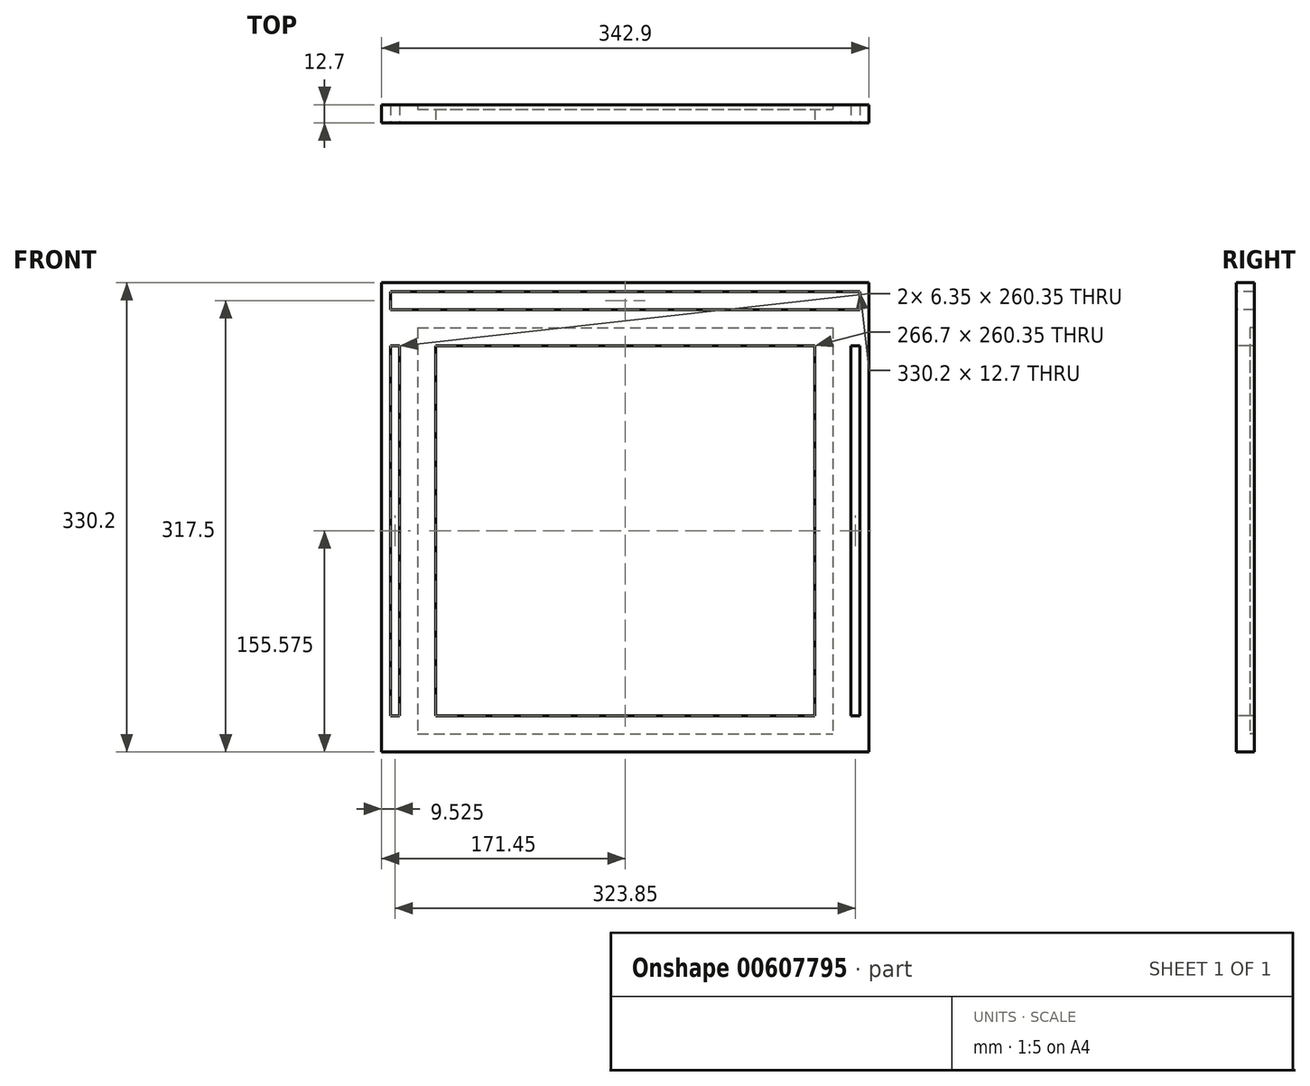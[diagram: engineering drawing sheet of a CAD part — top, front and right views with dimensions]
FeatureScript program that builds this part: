
annotation { "Feature Type Name" : "Feature", "Feature Type Description" : "" }
export const myFeature = defineFeature(function(context is Context, id is Id, definition is map)
    precondition{}
    {
        {
            var Q0;
            Q0=qCreatedBy(makeId("Front.planeOp"),FACE);
            var sketch = newSketch(context, id + "F0", { "sketchPlane" : qUnion([Q0])});
            skLineSegment(sketch, "E0.bottom", {"start": v(0, 0) * mm, "end": v(342.9, 0) * mm});
            skLineSegment(sketch, "E0.top", {"start": v(0, 330.2) * mm, "end": v(342.9, 330.2) * mm});
            skLineSegment(sketch, "E0.left", {"start": v(0, 0) * mm, "end": v(0, 330.2) * mm});
            skLineSegment(sketch, "E0.right", {"start": v(342.9, 0) * mm, "end": v(342.9, 330.2) * mm});
            skSolve(sketch);
        }
        {
            var Q0;
            Q0=makeQuery(id+"F0.imprint","IMPRINT",FACE,{"disambiguationData":[TD([[makeQuery(id+"F0.imprint","IMPRINT",EDGE,{"derivedFrom":sQuery(id+"F0.wireOp",EDGE,"E0.bottom")}),1.0]])]});
            extrude(context, id + "F1", {"entities" : qUnion([Q0]), "depth" : 12.7 * mm, "offsetDistance" : 25.4 * mm});
        }
        {
            var Q0;
            Q0=makeQuery(id+"F1.opExtrude","CAP_FACE",FACE,{"disambiguationData":[OSD([sQuery(id+"F0.wireOp",EDGE,"E0.bottom"),sQuery(id+"F0.wireOp",EDGE,"E0.top"),sQuery(id+"F0.wireOp",EDGE,"E0.left"),sQuery(id+"F0.wireOp",EDGE,"E0.right")])],"isStart":false});
            var sketch = newSketch(context, id + "F2", { "sketchPlane" : qUnion([Q0])});
            skLineSegment(sketch, "E1", {"start": v(0, 0) * mm, "end": v(25.4, 0) * mm});
            skLineSegment(sketch, "E2", {"start": v(25.4, 0) * mm, "end": v(25.4, 12.7) * mm});
            skLineSegment(sketch, "E3", {"start": v(25.4, 12.7) * mm, "end": v(317.5, 12.7) * mm});
            skLineSegment(sketch, "E4", {"start": v(317.5, 12.7) * mm, "end": v(317.5, 298.45) * mm});
            skLineSegment(sketch, "E5", {"start": v(317.5, 298.45) * mm, "end": v(25.4, 298.45) * mm});
            skLineSegment(sketch, "E6", {"start": v(25.4, 12.7) * mm, "end": v(25.4, 298.45) * mm});
            skSolve(sketch);
        }
        {
            var Q0;
            Q0=makeQuery(id+"F2.imprint","IMPRINT",FACE,{"disambiguationData":[TD([[makeQuery(id+"F2.imprint","IMPRINT",EDGE,{"derivedFrom":sQuery(id+"F2.wireOp",EDGE,"E3")}),1.0]])]});
            extrude(context, id + "F3", {"entities" : qUnion([Q0]), "operationType" : NewBodyOperationType.REMOVE, "oppositeDirection" : true, "depth" : 12.7 * mm, "offsetDistance" : 25.4 * mm});
        }
        {
            var Q0;
            Q0=makeQuery(id+"F1.opExtrude","CAP_FACE",FACE,{"disambiguationData":[OSD([sQuery(id+"F0.wireOp",EDGE,"E0.bottom"),sQuery(id+"F0.wireOp",EDGE,"E0.top"),sQuery(id+"F0.wireOp",EDGE,"E0.left"),sQuery(id+"F0.wireOp",EDGE,"E0.right")])],"isStart":false});
            var sketch = newSketch(context, id + "F4", { "sketchPlane" : qUnion([Q0])});
            skLineSegment(sketch, "E7", {"start": v(0, 330.2) * mm, "end": v(6.35, 330.2) * mm});
            skLineSegment(sketch, "E8", {"start": v(6.35, 330.2) * mm, "end": v(6.35, 323.85) * mm});
            skLineSegment(sketch, "E9", {"start": v(6.35, 323.85) * mm, "end": v(6.35, 311.15) * mm});
            skLineSegment(sketch, "E10", {"start": v(6.35, 311.15) * mm, "end": v(336.55, 311.15) * mm});
            skLineSegment(sketch, "E11", {"start": v(336.55, 311.15) * mm, "end": v(336.55, 323.85) * mm});
            skLineSegment(sketch, "E12", {"start": v(336.55, 323.85) * mm, "end": v(6.35, 323.85) * mm});
            skLineSegment(sketch, "E13", {"start": v(6.35, 311.15) * mm, "end": v(6.35, 285.75) * mm});
            skLineSegment(sketch, "E14", {"start": v(6.35, 285.75) * mm, "end": v(6.35, 25.4) * mm});
            skLineSegment(sketch, "E15", {"start": v(6.35, 25.4) * mm, "end": v(12.7, 25.4) * mm});
            skLineSegment(sketch, "E16", {"start": v(12.7, 25.4) * mm, "end": v(12.7, 285.75) * mm});
            skLineSegment(sketch, "E17", {"start": v(12.7, 285.75) * mm, "end": v(6.35, 285.75) * mm});
            skLineSegment(sketch, "E18", {"start": v(336.55, 311.15) * mm, "end": v(336.55, 285.75) * mm});
            skLineSegment(sketch, "E19", {"start": v(336.55, 285.75) * mm, "end": v(330.2, 285.75) * mm});
            skLineSegment(sketch, "E20", {"start": v(330.2, 285.75) * mm, "end": v(330.2, 25.4) * mm});
            skLineSegment(sketch, "E21", {"start": v(330.2, 25.4) * mm, "end": v(336.55, 25.4) * mm});
            skLineSegment(sketch, "E22", {"start": v(336.55, 25.4) * mm, "end": v(336.55, 285.75) * mm});
            skSolve(sketch);
        }
        {
            var Q0;
            Q0=makeQuery(id+"F4.imprint","IMPRINT",FACE,{"disambiguationData":[TD([[makeQuery(id+"F4.imprint","IMPRINT",EDGE,{"derivedFrom":sQuery(id+"F4.wireOp",EDGE,"E9")}),1.0]])]});
            var Q1;
            Q1=makeQuery(id+"F4.imprint","IMPRINT",FACE,{"disambiguationData":[TD([[makeQuery(id+"F4.imprint","IMPRINT",EDGE,{"derivedFrom":sQuery(id+"F4.wireOp",EDGE,"E14")}),1.0]])]});
            var Q2;
            Q2=makeQuery(id+"F4.imprint","IMPRINT",FACE,{"disambiguationData":[TD([[makeQuery(id+"F4.imprint","IMPRINT",EDGE,{"derivedFrom":sQuery(id+"F4.wireOp",EDGE,"E19")}),1.0]])]});
            extrude(context, id + "F5", {"entities" : qUnion([Q0, Q1, Q2]), "operationType" : NewBodyOperationType.REMOVE, "oppositeDirection" : true, "depth" : 12.7 * mm, "offsetDistance" : 25.4 * mm});
        }
        {
            var Q0;
            Q0=makeQuery(id+"F3.boolean.opBoolean","COPY",FACE,{"derivedFrom":makeQuery(id+"F3.opExtrude","SWEPT_FACE",FACE,{"disambiguationData":[OSD([sQuery(id+"F2.wireOp",EDGE,"E3")])]})});
            var sketch = newSketch(context, id + "F6", { "sketchPlane" : qUnion([Q0])});
            skLineSegment(sketch, "E23.bottom", {"start": v(25.4, -12.7) * mm, "end": v(317.5, -12.7) * mm});
            skLineSegment(sketch, "E23.top", {"start": v(25.4, -3.18) * mm, "end": v(317.5, -3.18) * mm});
            skLineSegment(sketch, "E23.left", {"start": v(25.4, -12.7) * mm, "end": v(25.4, -3.18) * mm});
            skLineSegment(sketch, "E23.right", {"start": v(317.5, -12.7) * mm, "end": v(317.5, -3.18) * mm});
            skSolve(sketch);
        }
        {
            var Q0;
            Q0=makeQuery(id+"F6.imprint","IMPRINT",FACE,{"disambiguationData":[TD([[makeQuery(id+"F6.imprint","IMPRINT",EDGE,{"derivedFrom":sQuery(id+"F6.wireOp",EDGE,"E23.bottom")}),1.0]])]});
            extrude(context, id + "F7", {"entities" : qUnion([Q0]), "operationType" : NewBodyOperationType.ADD, "depth" : 12.7 * mm, "offsetDistance" : 25.4 * mm});
        }
        {
            var Q0;
            Q0=makeQuery(id+"F3.boolean.opBoolean","COPY",FACE,{"derivedFrom":makeQuery(id+"F3.opExtrude","SWEPT_FACE",FACE,{"disambiguationData":[OSD([sQuery(id+"F2.wireOp",EDGE,"E5")])]})});
            var sketch = newSketch(context, id + "F8", { "sketchPlane" : qUnion([Q0])});
            skLineSegment(sketch, "E24.bottom", {"start": v(25.4, 12.7) * mm, "end": v(317.5, 12.7) * mm});
            skLineSegment(sketch, "E24.top", {"start": v(25.4, 3.18) * mm, "end": v(317.5, 3.18) * mm});
            skLineSegment(sketch, "E24.left", {"start": v(25.4, 12.7) * mm, "end": v(25.4, 3.18) * mm});
            skLineSegment(sketch, "E24.right", {"start": v(317.5, 12.7) * mm, "end": v(317.5, 3.18) * mm});
            skSolve(sketch);
        }
        {
            var Q0;
            Q0=makeQuery(id+"F8.imprint","IMPRINT",FACE,{"disambiguationData":[TD([[makeQuery(id+"F8.imprint","IMPRINT",EDGE,{"derivedFrom":sQuery(id+"F8.wireOp",EDGE,"E24.bottom")}),1.0]])]});
            extrude(context, id + "F9", {"entities" : qUnion([Q0]), "operationType" : NewBodyOperationType.ADD, "depth" : 12.7 * mm, "offsetDistance" : 25.4 * mm});
        }
        {
            var Q0;
            Q0=makeQuery(id+"F3.boolean.opBoolean","COPY",FACE,{"derivedFrom":makeQuery(id+"F3.opExtrude","SWEPT_FACE",FACE,{"disambiguationData":[OSD([sQuery(id+"F2.wireOp",EDGE,"E4")])]})});
            var sketch = newSketch(context, id + "F10", { "sketchPlane" : qUnion([Q0])});
            skLineSegment(sketch, "E25.bottom", {"start": v(12.7, 285.75) * mm, "end": v(3.17, 285.75) * mm});
            skLineSegment(sketch, "E25.top", {"start": v(12.7, 25.4) * mm, "end": v(3.17, 25.4) * mm});
            skLineSegment(sketch, "E25.left", {"start": v(12.7, 285.75) * mm, "end": v(12.7, 25.4) * mm});
            skLineSegment(sketch, "E25.right", {"start": v(3.17, 285.75) * mm, "end": v(3.17, 25.4) * mm});
            skSolve(sketch);
        }
        {
            var Q0;
            Q0=makeQuery(id+"F10.imprint","IMPRINT",FACE,{"disambiguationData":[TD([[makeQuery(id+"F10.imprint","IMPRINT",EDGE,{"derivedFrom":sQuery(id+"F10.wireOp",EDGE,"E25.bottom")}),-1.0]])]});
            extrude(context, id + "F11", {"entities" : qUnion([Q0]), "operationType" : NewBodyOperationType.ADD, "depth" : 12.7 * mm, "offsetDistance" : 25.4 * mm});
        }
        {
            var Q0;
            Q0=makeQuery(id+"F3.boolean.opBoolean","COPY",FACE,{"derivedFrom":makeQuery(id+"F3.opExtrude","SWEPT_FACE",FACE,{"disambiguationData":[OSD([sQuery(id+"F2.wireOp",EDGE,"E6")])]})});
            var sketch = newSketch(context, id + "F12", { "sketchPlane" : qUnion([Q0])});
            skLineSegment(sketch, "E26.bottom", {"start": v(-12.7, 285.75) * mm, "end": v(-3.17, 285.75) * mm});
            skLineSegment(sketch, "E26.top", {"start": v(-12.7, 25.4) * mm, "end": v(-3.17, 25.4) * mm});
            skLineSegment(sketch, "E26.left", {"start": v(-12.7, 285.75) * mm, "end": v(-12.7, 25.4) * mm});
            skLineSegment(sketch, "E26.right", {"start": v(-3.17, 285.75) * mm, "end": v(-3.17, 25.4) * mm});
            skSolve(sketch);
        }
        {
            var Q0;
            Q0=makeQuery(id+"F12.imprint","IMPRINT",FACE,{"disambiguationData":[TD([[makeQuery(id+"F12.imprint","IMPRINT",EDGE,{"derivedFrom":sQuery(id+"F12.wireOp",EDGE,"E26.bottom")}),1.0]])]});
            extrude(context, id + "F13", {"entities" : qUnion([Q0]), "operationType" : NewBodyOperationType.ADD, "depth" : 12.7 * mm, "offsetDistance" : 25.4 * mm});
        }
    });
